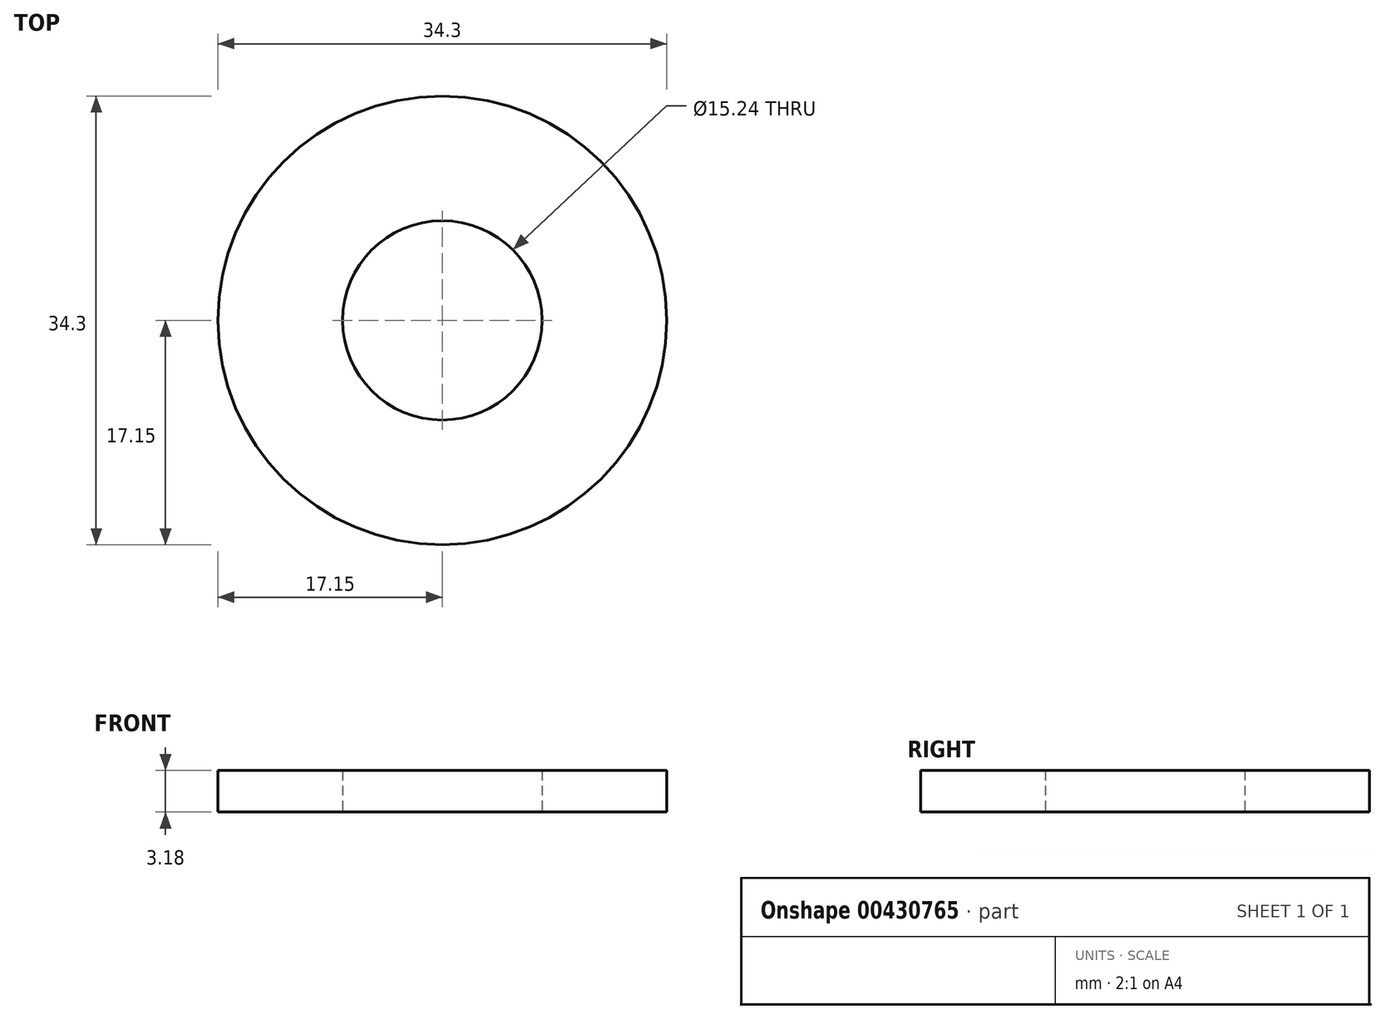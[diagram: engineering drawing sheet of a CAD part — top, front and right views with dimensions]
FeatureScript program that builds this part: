
annotation { "Feature Type Name" : "Feature", "Feature Type Description" : "" }
export const myFeature = defineFeature(function(context is Context, id is Id, definition is map)
    precondition{}
    {
        {
            var Q0;
            Q0=qCreatedBy(makeId("Top.planeOp"),FACE);
            var sketch = newSketch(context, id + "F0", { "sketchPlane" : qUnion([Q0])});
            skCircle(sketch, "E0", {"center": v(0, 0) * mm, "radius": 17.15 * mm});
            skCircle(sketch, "E1", {"center": v(0, 0) * mm, "radius": 7.62 * mm});
            skSolve(sketch);
        }
        {
            var Q0;
            Q0=makeQuery(id+"F0.imprint","IMPRINT",FACE,{"disambiguationData":[TD([[makeQuery(id+"F0.imprint","IMPRINT",EDGE,{"derivedFrom":sQuery(id+"F0.wireOp",EDGE,"E0")}),1.0]])]});
            extrude(context, id + "F1", {"entities" : qUnion([Q0]), "depth" : 3.17 * mm, "offsetDistance" : 25.4 * mm});
        }
    });
